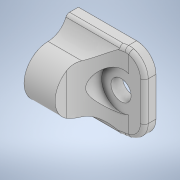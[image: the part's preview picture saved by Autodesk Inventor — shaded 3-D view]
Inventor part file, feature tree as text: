
AUTODESK INVENTOR PART (.ipt)
format: ipt  version: 2020 (Build 240168000, 168)  size: 219,136 bytes
history: native  units: mm
features: extrude x4, sketch x4, fillet x3
ambient origin geometry x8: Origin, YZ Plane, XZ Plane, XY Plane, X Axis, Y Axis, Z Axis, Center Point
bodies: Solid1 (feature_tree)
feature tree (11):
  extrude  "Extrusion1"  Depth=5.0mm
  extrude  "Extrusion2"  Depth=5.2mm
  fillet  "Fillet1"  Radius=3.0mm
  extrude  "Extrusion3"  Depth=5.0mm
  fillet  "Fillet2"  Radius=3.0mm
  extrude  "Extrusion4"  Depth=10.0mm
  fillet  "Fillet3"  Radius=10.5mm
  sketch  "Sketch1"  dims[d2=5.0mm d3=5.0mm]
  sketch  "Sketch2"  dims[d4=6.0mm d5=5.2mm d6=3.0mm d7=0.0mm]
  sketch  "Sketch3"  dims[d10=8.0mm d11=0.0mm d12=5.0mm d13=3.0mm d14=0.0mm]
  sketch  "Sketch4"  dims[d15=8.0mm d16=10.0mm d17=10.5mm d18=0.0mm d19=1.0mm]
